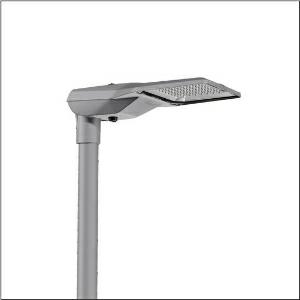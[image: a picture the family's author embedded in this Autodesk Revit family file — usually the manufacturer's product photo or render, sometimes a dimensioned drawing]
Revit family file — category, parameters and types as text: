
# Revit family: streetlight_sl_21_iq_midi___st1_0a_5xe3d21y08mb_afa7
name_source: partatom
category: Lighting Fixtures
units: mm (PartAtom-declared; Revit-internal decimal feet)

## family parameters
Cut with Voids When Loaded = No
Host = Face
Light Source = No
Part Type = Normal
Room Calculation Point = No
Round Connector Dimension = Use Diameter
Shared = No

## types (1)
- --- (1 x LED, 14710 lm, 129.3 W, 2200K)
    Apparent Load = 129 VA
    CIE Flux Codes = 37 72 97 100 100
    Color Rendering = 70
    Color Temperature = 2200K
    Default Elevation = 1800 mm
    Description = Streetlight SL 21 iQ midi, mast luminaire, primary light control with lens, of PMMA, primary optical cover: cover, of toughened safety glass, transparent, light distribution: ST1.0a, light emission: direct distribution, primary light characteristic: asymmetric, installation type: post-top, side-entry, LED, High Power LED, rated luminous flux: 14.710lm, luminous efficacy: 114lm/W, light colour: 722, colour temperature: 2200K, control gear: iQ-Street Remote, D4i with power reduction, control: pre-setting: logarithmic dimming characteristic, Street-Remote, Auto-Match, Temp-Guard, Lumen-Switch, Night-Set, Smart-Wire, Light-Fading, Desk-Remote (wireless, voltage-free reading and setting of iQ features in the workshop via application-optimized NFC function/RFID function), optimised constant luminous flux control (CLO 2.0), mains connection: 230..240V, AC, 50/60Hz, start of lifetime: 129W, end of service life: 142W, reduction: 56W, luminaire housing, of diecast aluminium, powder-coated, Siteco® metallic grey (DB 702S), corrosivity category C5 mid according to DIN EN ISO 12944, please order mast flange separately, inclination adjustable: 0°, 5°, 10°, 15°, sealing non-destructively replaceable, multi-level sealing system, length: 644mm, width: 335mm, height: 110mm, mast flange for spigot size: 42mm (side-entry): 5XC10008XM4, 60/48mm (side-entry/post-top): 5XC10108XM2, 76/60mm (side-entry/post-top): 5XC10108XM1, mounting height: 4..8m, Smart Interface below and above, protection rating (complete): IP66, insulation class (complete): insulation class II (safety insulation), certification: CE, ENEC, ENEC+, VDE, impact resistance: IK10, permissible operating ambient temperature for outdoor applications: -40..+50°C, standard-compliant lighting for roads and squares, packaging unit: 1 piece

Light Distribution: ST1.0a
    Height = 111 mm
    Lamp = 1 x LED
    Lamp Light Flux = 14710 lm
    Lamp Power = 129.3 W
    Lamp count = 1
    Length = 644 mm
    Luminous efficacy = 114 lm/W
    Manufacturer = Siteco
    ModVariant = No
    Model = 5XE3D21Y08MB
    Number of Poles = 1
    OnlyDefault = Yes
    Power Factor = 1
    Product Name = Streetlight SL 21 iQ midi | ST1.0a
    Product group = mast luminaire | pylon top
    ProductGroupID = 6100
    Protection Class = Protection class II
    Protection Degree = IP 66
    RLX_Detail_Level = 1
    RLX_Emergency_Light_Flux = 0 lm
    RLX_Emergency_Type = 0
    RLX_Emergency_Type_DB = No
    RlxData = <blob elided: 90845 chars, md5=6704b8ec>
    Socket = socket
    Standby Power = 0 W
    System Light Flux = 14710 lm
    System Power = 129 W
    Type Comments = factory setting: luminous flux: 100 % | dim-lin: 254 | 672 mA
    Type Image = l_1004304.jpg
    URL = http://relux.com
    VarID = @adj_136083
    Voltage = 0 V
    Weight = 0.00 kg
    Width = 336 mm

## geometry (parser evidence)
native form markers: Blend x4, Sweep x13
no freeform markers — native parametric forms only
